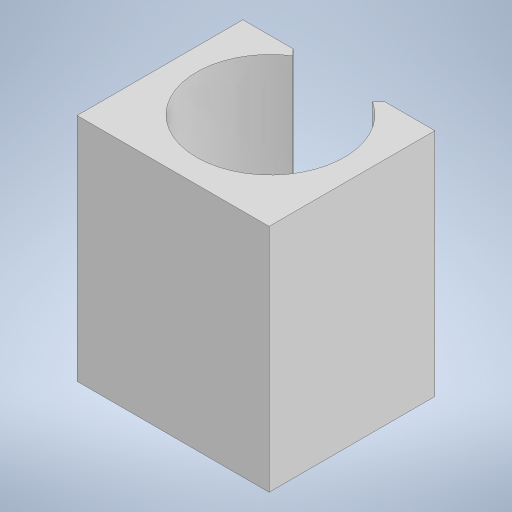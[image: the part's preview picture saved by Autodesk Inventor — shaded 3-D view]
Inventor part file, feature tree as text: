
AUTODESK INVENTOR PART (.ipt)
format: ipt  version: 2024 (Build 280153000, 153)  size: 215,040 bytes
history: native  units: mm
features: extrude x2, sketch x2
ambient origin geometry x8: Origin, YZ Plane, XZ Plane, XY Plane, X Axis, Y Axis, Z Axis, Center Point
bodies: Solid1 (feature_tree)
feature tree (4):
  extrude  "Extrusion1"  Depth=50.0mm TaperAngle=0.0deg
  extrude  "Extrusion3"  Depth=2.0mm
  sketch  "Sketch1"  dims[d0=0.0mm d1=32.1mm d2=0.0mm d3=0.0mm d4=50.0mm d5=0.0mm]
  sketch  "Sketch5"  dims[d16=2.0mm d17=2.0mm d18=100.0mm d19=0.0mm]
